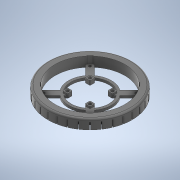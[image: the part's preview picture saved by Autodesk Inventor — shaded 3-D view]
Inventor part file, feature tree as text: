
AUTODESK INVENTOR PART (.ipt)
format: ipt  version: 2020 (Build 240168000, 168)  size: 1,389,568 bytes
history: native  units: mm
features: projected_geometry x13, extrude x12, sketch x10, pattern_circular x5, fillet x4, other x1
ambient origin geometry x8: Origin, YZ Plane, XZ Plane, XY Plane, X Axis, Y Axis, Z Axis, Center Point
bodies: Body1 (feature_tree)
feature tree (45):
  other  "Твердое тело1"
  sketch  "Эскиз1"
  extrude  "Выдавливание1"  Depth=88.0mm
  extrude  "Выдавливание2"  Depth=5.7mm
  pattern_circular  "Круговой массив1"  [2 undecoded]
  extrude  "Выдавливание3"  Depth=5.4mm
  fillet  "Сопряжение1"  Radius=98.0mm
  extrude  "Выдавливание4"  Depth=84.0mm
  pattern_circular  "Круговой массив2"  [2 undecoded]
  fillet  "Сопряжение2"  Radius=98.0mm
  extrude  "Выдавливание5"  Depth=84.0mm
  pattern_circular  "Круговой массив3"  [2 undecoded]
  extrude  "Выдавливание6"  Depth=10.0mm TaperAngle=0.0deg
  fillet  "Сопряжение3"  Radius=320.0mm
  sketch  "Эскиз6"
  extrude  "Выдавливание7"  Depth=2.0mm
  pattern_circular  "Круговой массив4"  [2 undecoded]
  extrude  "Выдавливание8"  Depth=1.6mm TaperAngle=0.0deg
  extrude  "Выдавливание9"  Depth=2.0mm
  pattern_circular  "Круговой массив5"  [2 undecoded]
  fillet  "Сопряжение4"  Radius=320.0mm
  sketch  "Эскиз9"
  extrude  "Выдавливание10"  Depth=0.5mm
  extrude  "Выдавливание11"  Depth=78.0mm
  extrude  "Выдавливание12"  TaperAngle=135.0deg  [1 undecoded]
  sketch  "Эскиз2"
  sketch  "Эскиз3"
  projected_geometry  "Спроецированная петля1"
  sketch  "Эскиз4"
  projected_geometry  "Спроецированная петля2"
  sketch  "Эскиз5"
  projected_geometry  "Спроецированная петля3"
  projected_geometry  "Спроецированная петля4"
  projected_geometry  "Спроецированная петля5"
  projected_geometry  "Спроецированная петля6"
  projected_geometry  "Спроецированная петля7"
  sketch  "Эскиз7"
  sketch  "Эскиз8"
  projected_geometry  "Спроецированная петля8"
  projected_geometry  "Спроецированная петля9"
  projected_geometry  "Спроецированная петля10"
  projected_geometry  "Спроецированная петля11"
  projected_geometry  "Спроецированная петля12"
  projected_geometry  "Спроецированная петля13"
  sketch  "Эскиз10"
note: 11 required parameter values undecoded (feature->parameter linkage not recoverable at this tier; creation-order binding heuristic only, values carry confidence <= 0.55)
